# Revit family: Sanitary_Shower-screens_Duscholux_D3_Mode_Separator-Fixed-panel-shower
name_source: partatom
category: Aparatos sanitarios
units: mm (PartAtom-declared; Revit-internal decimal feet)

## family parameters
Compartido = No
Corte con vacíos al cargar = No
Cota de conector redondo = Diámetro de uso
Número OmniClass = 23.45.00.00
Punto de cálculo de habitación = No
Se basa en plano de trabajo = No
Siempre vertical = Sí
Tipo de pieza = Normal
Título OmniClass = Sanitary, Laundry, and Cleaning Equipment

## types (2) — shared parameters
Certified Quality UNE EN 14428 = http://www.duscholux.es
Components = Eropean components
Configuration enclosure = http://configuratumampara.duscholux.es
Código de montaje = C1030200
Descripción = Fixed separator (Shower)
Environmental Management ISO 14001 = ECOEMBES Certificate
Fabricante = Duscholux Ibérica, S.A.
Fact Sheet = https://duscholux.es
Glass Material = Glass_Material-Duscholux
Glass in Building UNE EN 12150 = CE Conformity marking
Height = 2000 mm  [stored 6.56168 ft]
Image = https://duscholux.es
Lenght Support = 800 mm  [stored 2.62467 ft]
Maintenance and Cleaning = http://www.duscholux.es
Min/Max Width = 1000 mm  [stored 3.28084 ft]
Modelo = D3 Mode
Offset Support = 50 mm  [stored 0.164042 ft]
Opening System = Fixed panel
Opening System Image = http://blob.duscholux.es
Products = http://www.duscholux.es
Ref. = D3M
Series = D3
Technical Inspection Certificate (Applus) = http://www.duscholux.es
Thickness Safety Glass = 8 mm  [stored 0.0262467 ft]
URL = http://www.duscholux.es
Width = 1000 mm  [stored 3.28084 ft]

## per-type parameters (varying)
| type | Frame Material |
| Platinum Aluminium Finish | Anodized Aluminium_Duscholux Material-Platinum Finish |
| Black Aluminium Finish | Anodized Aluminium_Duscholux Material-Black Finish |

note: [stored X ft] marks values corroborated as IEEE doubles in the binary element streams (Revit-internal decimal feet)
